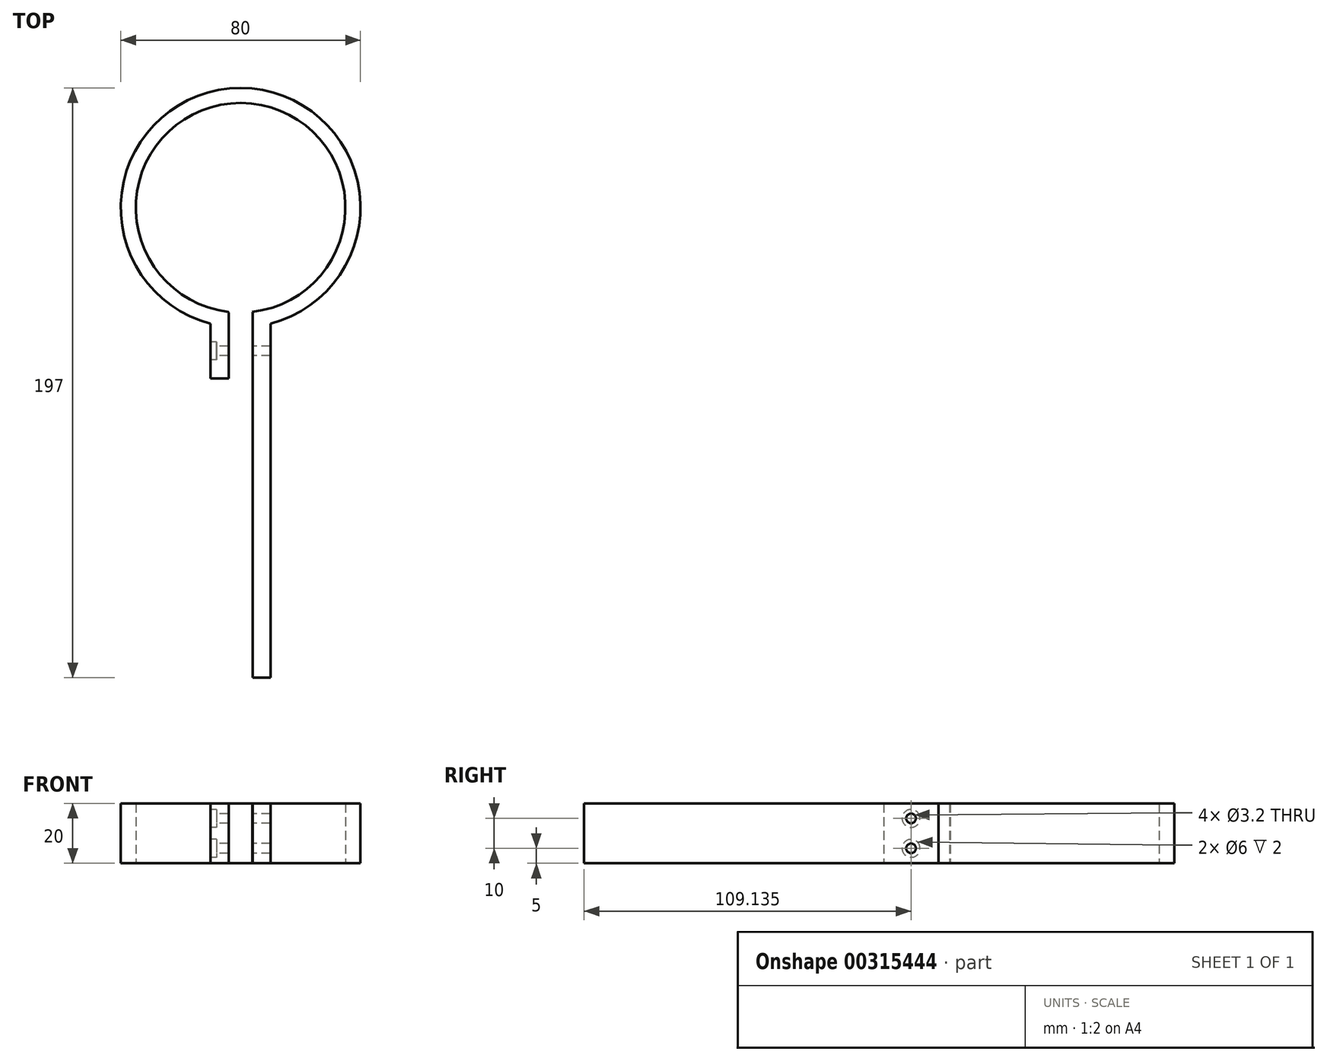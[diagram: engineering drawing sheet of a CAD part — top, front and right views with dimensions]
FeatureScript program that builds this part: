
annotation { "Feature Type Name" : "Feature", "Feature Type Description" : "" }
export const myFeature = defineFeature(function(context is Context, id is Id, definition is map)
    precondition{}
    {
        {
            var Q0;
            Q0=qCreatedBy(makeId("Top.planeOp"),FACE);
            var sketch = newSketch(context, id + "F0", { "sketchPlane" : qUnion([Q0])});
            skPoint(sketch, "E0.middle", {"position": v(0, 0) * mm});
            skArc(sketch, "E1", {"start": v(10, 16.46) * mm, "mid": v(0, 85) * mm, "end": v(-10, 16.46) * mm});
            skLineSegment(sketch, "E2", {"start": v(10, 11.27) * mm, "end": v(10, 11.27) * mm});
            skArc(sketch, "E3", {"start": v(-10, 16.46) * mm, "mid": v(-7.11, 15.73) * mm, "end": v(-4.18, 15.25) * mm});
            skLineSegment(sketch, "E4", {"start": v(10, 16.46) * mm, "end": v(10, -7) * mm});
            skLineSegment(sketch, "E5", {"start": v(-10, 16.46) * mm, "end": v(-10, -7.38) * mm});
            skLineSegment(sketch, "E6", {"start": v(-10, 11.27) * mm, "end": v(-10, 11.27) * mm});
            skArc(sketch, "E7", {"start": v(10, 11.27) * mm, "mid": v(0, 90) * mm, "end": v(-10, 11.27) * mm});
            skLineSegment(sketch, "E8.0", {"start": v(10, -7) * mm, "end": v(4, -7) * mm});
            skLineSegment(sketch, "E9.0", {"start": v(4, -7) * mm, "end": v(4, 15) * mm});
            skLineSegment(sketch, "E10.MirrorCS", {"start": v(-4, -7) * mm, "end": v(-4, 15) * mm});
            skLineSegment(sketch, "E11", {"start": v(-4.18, 15.25) * mm, "end": v(-4.18, 15.25) * mm});
            skArc(sketch, "E12", {"start": v(3.93, 15.22) * mm, "mid": v(7, 15.7) * mm, "end": v(10, 16.46) * mm});
            skLineSegment(sketch, "E13", {"start": v(-4, -7) * mm, "end": v(-10, -7) * mm});
            skLineSegment(sketch, "E14", {"start": v(3.93, 15.22) * mm, "end": v(4, 15) * mm});
            skLineSegment(sketch, "E15", {"start": v(-4.18, 15.25) * mm, "end": v(-4, 15) * mm});
            skSolve(sketch);
        }
        {
            var Q0;
            {var subQ0=sQuery(id+"F0.wireOp",EDGE,"E1");Q0=makeQuery(id+"F0.imprint","IMPRINT",FACE,{"disambiguationData":[TD([[makeQuery(id+"F0.imprint","IMPRINT",EDGE,{"derivedFrom":subQ0}),-1.0]])]});}
            var Q1;
            {var subQ3=sQuery(id+"F0.wireOp",EDGE,"E3");Q1=makeQuery(id+"F0.imprint","IMPRINT",FACE,{"disambiguationData":[TD([[makeQuery(id+"F0.imprint","IMPRINT",EDGE,{"derivedFrom":subQ3}),-1.0]])]});}
            var Q2;
            {var subQ0=sQuery(id+"F0.wireOp",EDGE,"E8.0");Q2=makeQuery(id+"F0.imprint","IMPRINT",FACE,{"disambiguationData":[TD([[makeQuery(id+"F0.imprint","IMPRINT",EDGE,{"derivedFrom":subQ0}),-1.0]])]});}
            extrude(context, id + "F1", {"entities" : qUnion([Q0, Q1, Q2]), "depth" : 20 * mm, "offsetDistance" : 25 * mm});
        }
        {
            var Q0;
            Q0=makeQuery(id+"F1.opExtrude","SWEPT_FACE",FACE,{"disambiguationData":[OSD([sQuery(id+"F0.wireOp",EDGE,"E5")])]});
            var sketch = newSketch(context, id + "F2", { "sketchPlane" : qUnion([Q0])});
            skLineSegment(sketch, "E16", {"start": v(-2.14, 20) * mm, "end": v(-2.14, 10) * mm});
            skLineSegment(sketch, "E17", {"start": v(7, 10) * mm, "end": v(-2.14, 10) * mm});
            skLineSegment(sketch, "E18", {"start": v(-2.14, 10) * mm, "end": v(-11.27, 10) * mm});
            skLineSegment(sketch, "E19", {"start": v(-2.14, 10) * mm, "end": v(-2.14, 0) * mm});
            skPoint(sketch, "E20", {"position": v(-2.14, 5) * mm});
            skPoint(sketch, "E21", {"position": v(-2.14, 15) * mm});
            skSolve(sketch);
        }
        {
            var Q0;
            Q0=sQuery(id+"F2.wireOp",VERTEX,"E20");
            var Q1;
            Q1=sQuery(id+"F2.wireOp",VERTEX,"E21");
            var Q2;
            Q2=makeQuery(id+"F1.opExtrude","SWEPT_BODY",BODY,{"disambiguationData":[OSD([sQuery(id+"F0.wireOp",EDGE,"E1"),sQuery(id+"F0.wireOp",EDGE,"E3"),sQuery(id+"F0.wireOp",EDGE,"E4"),sQuery(id+"F0.wireOp",EDGE,"E5"),sQuery(id+"F0.wireOp",EDGE,"E7"),sQuery(id+"F0.wireOp",EDGE,"E8.0"),sQuery(id+"F0.wireOp",EDGE,"E9.0"),sQuery(id+"F0.wireOp",EDGE,"E10.MirrorCS"),sQuery(id+"F0.wireOp",EDGE,"E12"),sQuery(id+"F0.wireOp",EDGE,"E13"),sQuery(id+"F0.wireOp",EDGE,"E14"),sQuery(id+"F0.wireOp",EDGE,"E15")])]});
            hole(context, id + "F3", {"style" : HoleStyle.C_BORE, "endStyle" : HoleEndStyle.THROUGH, "holeDiameter" : 3.2 * mm, "cBoreDiameter" : 6 * mm, "cBoreDepth" : 2 * mm, "isTappedThrough" : true, "tappedDepth" : 12 * mm, "tapClearance" : 3, "locations" : qUnion([Q0, Q1]), "scope" : qUnion([Q2])});
        }
        {
            var Q0;
            Q0=makeQuery(id+"F1.opExtrude","SWEPT_FACE",FACE,{"disambiguationData":[OSD([sQuery(id+"F0.wireOp",EDGE,"E4")])]});
            var sketch = newSketch(context, id + "F4", { "sketchPlane" : qUnion([Q0])});
            skLineSegment(sketch, "E22.bottom", {"start": v(-7, 20) * mm, "end": v(-107, 20) * mm});
            skLineSegment(sketch, "E22.top", {"start": v(-7, 0) * mm, "end": v(-107, 0) * mm});
            skLineSegment(sketch, "E22.left", {"start": v(-7, 20) * mm, "end": v(-7, 0) * mm});
            skLineSegment(sketch, "E22.right", {"start": v(-107, 20) * mm, "end": v(-107, 0) * mm});
            skSolve(sketch);
        }
        {
            var Q0;
            Q0=makeQuery(id+"F4.imprint","IMPRINT",FACE,{"disambiguationData":[TD([[makeQuery(id+"F4.imprint","IMPRINT",EDGE,{"derivedFrom":sQuery(id+"F4.wireOp",EDGE,"E22.bottom")}),1.0]])]});
            extrude(context, id + "F5", {"entities" : qUnion([Q0]), "operationType" : NewBodyOperationType.ADD, "oppositeDirection" : true, "depth" : 6 * mm, "offsetDistance" : 25 * mm});
        }
    });
